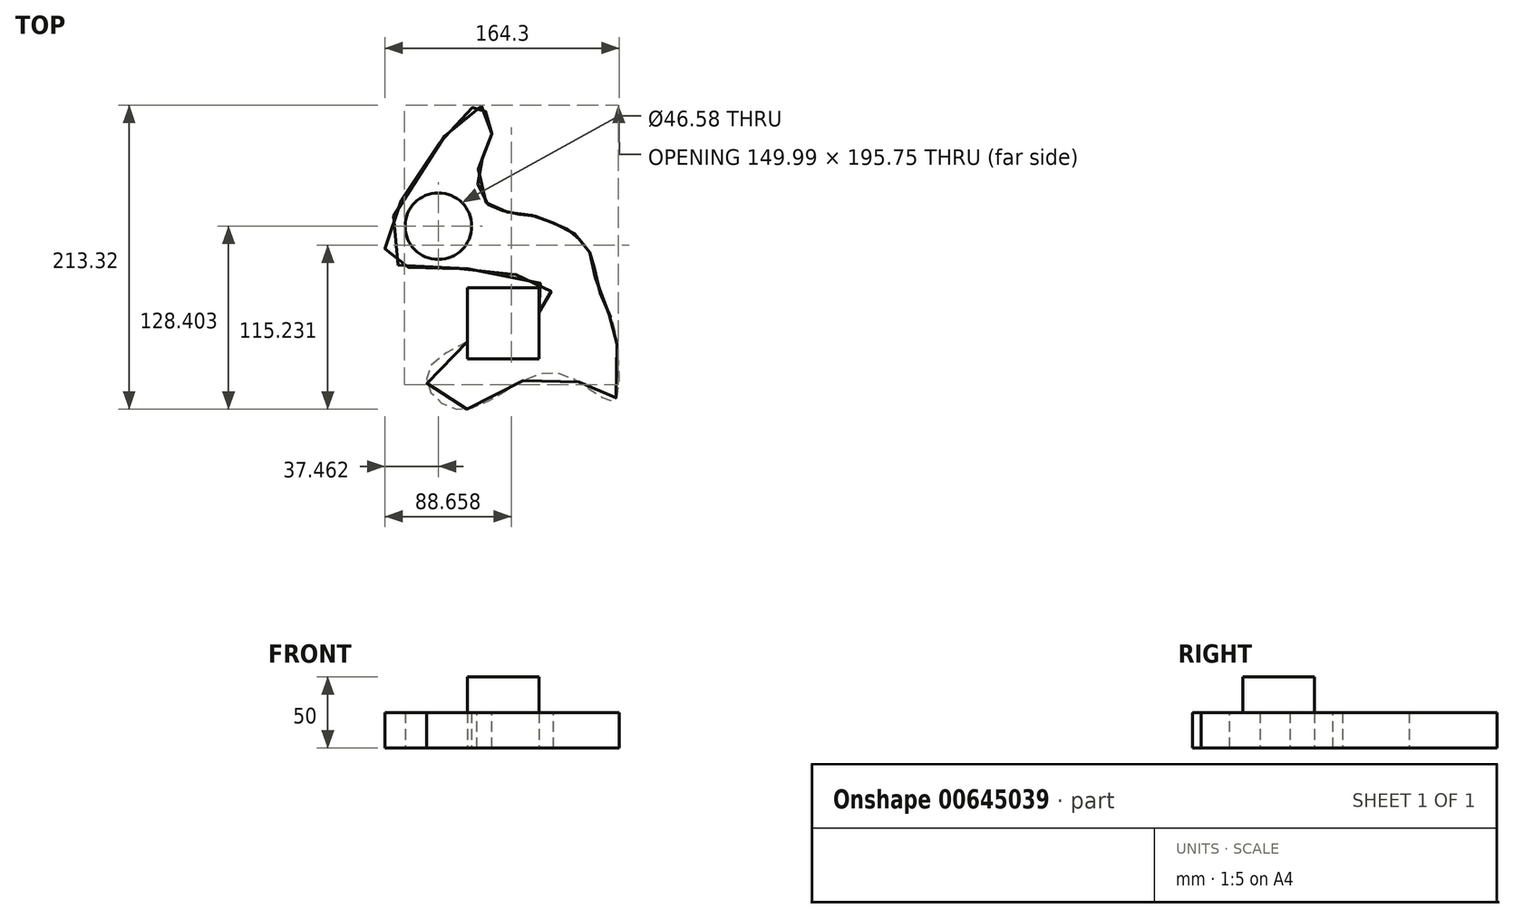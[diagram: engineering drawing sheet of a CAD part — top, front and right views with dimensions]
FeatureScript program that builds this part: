
annotation { "Feature Type Name" : "Feature", "Feature Type Description" : "" }
export const myFeature = defineFeature(function(context is Context, id is Id, definition is map)
    precondition{}
    {
        {
            var Q0;
            Q0=qCreatedBy(makeId("Top.planeOp"),FACE);
            var sketch = newSketch(context, id + "F0", { "sketchPlane" : qUnion([Q0])});
            skLineSegment(sketch, "E0.bottom", {"start": v(-13.47, 15.24) * mm, "end": v(36.53, 15.24) * mm});
            skLineSegment(sketch, "E0.top", {"start": v(-13.47, -34.76) * mm, "end": v(36.53, -34.76) * mm});
            skLineSegment(sketch, "E0.left", {"start": v(-13.47, 15.24) * mm, "end": v(-13.47, -34.76) * mm});
            skLineSegment(sketch, "E0.right", {"start": v(36.53, 15.24) * mm, "end": v(36.53, -34.76) * mm});
            skSolve(sketch);
        }
        {
            var Q0;
            Q0 = qSketchRegion(id + "F0", true);
            extrude(context, id + "F1", {"entities" : qUnion([Q0]), "depth" : 50 * mm, "offsetDistance" : 25 * mm});
        }
        {
            var Q0;
            Q0=qCreatedBy(makeId("Top.planeOp"),FACE);
            var sketch = newSketch(context, id + "F2", { "sketchPlane" : qUnion([Q0])});
            skFitSpline(sketch, "E1", {"points": [v(89.23, -63.32) * mm, v(89.52, -14.41) * mm, v(86.61, -5.39) * mm, v(76.13, 21.98) * mm, v(74.1, 36.83) * mm, v(68.56, 44.4) * mm, v(61.28, 53.42) * mm, v(53.13, 57.8) * mm, v(39.45, 63.61) * mm, v(31.88, 65.94) * mm, v(20.53, 66.82) * mm, v(9.46, 69.73) * mm, v(0, 74.39) * mm, v(-6.55, 95.64) * mm, v(3.35, 121.84) * mm, v(-2.18, 140.77) * mm, v(-9.46, 141.93) * mm, v(-71.18, 41.2) * mm, v(0, 27.8) * mm, v(45.85, 5.39) * mm, v(-40.61, -41.78) * mm, v(-18.2, -70.02) * mm, v(47.3, -44.1) * mm, v(89.23, -63.32) * mm]});
            skSolve(sketch);
        }
        {
            var Q0;
            Q0 = qSketchRegion(id + "F2", true);
            extrude(context, id + "F3", {"entities" : qUnion([Q0]), "operationType" : NewBodyOperationType.ADD, "depth" : 25 * mm, "offsetDistance" : 25 * mm});
        }
        {
            var Q0;
            Q0=qCreatedBy(makeId("Top.planeOp"),FACE);
            var sketch = newSketch(context, id + "F4", { "sketchPlane" : qUnion([Q0])});
            skCircle(sketch, "E2", {"center": v(-33.92, 58.37) * mm, "radius": 23.3 * mm});
            skSolve(sketch);
        }
        {
            var Q0;
            Q0 = qSketchRegion(id + "F4", true);
            extrude(context, id + "F5", {"entities" : qUnion([Q0]), "operationType" : NewBodyOperationType.REMOVE, "depth" : 50 * mm, "offsetDistance" : 25 * mm});
        }
    });
